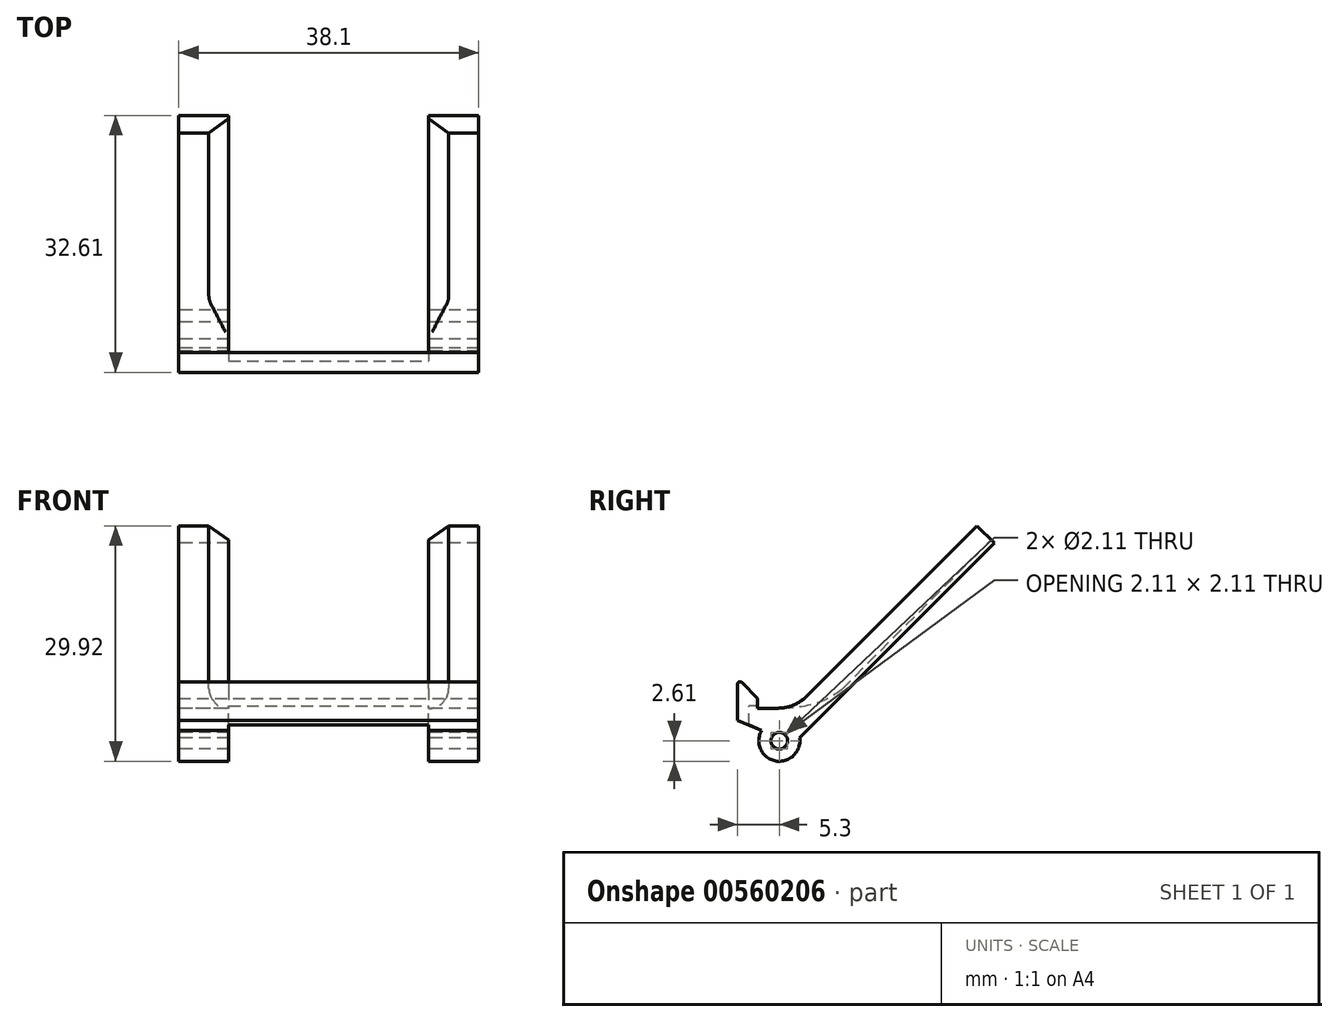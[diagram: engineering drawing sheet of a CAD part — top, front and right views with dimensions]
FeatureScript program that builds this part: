
annotation { "Feature Type Name" : "Feature", "Feature Type Description" : "" }
export const myFeature = defineFeature(function(context is Context, id is Id, definition is map)
    precondition{}
    {
        {
            var Q0;
            Q0=qCreatedBy(makeId("Right.planeOp"),FACE);
            var sketch = newSketch(context, id + "F0", { "sketchPlane" : qUnion([Q0])});
            skCircle(sketch, "E0", {"center": v(0, 0) * mm, "radius": 1.05 * mm});
            skArc(sketch, "E1.0", {"start": v(-2.24, 1.34) * mm, "mid": v(-0.5, -2.56) * mm, "end": v(2.58, 0.38) * mm});
            skLineSegment(sketch, "E2", {"start": v(0, 0) * mm, "end": v(18.4, 0) * mm, "construction": true});
            skLineSegment(sketch, "E3.0", {"start": v(1.94, 4.14) * mm, "end": v(25.1, 27.3) * mm});
            skLineSegment(sketch, "E4.0", {"start": v(2.58, 0.38) * mm, "end": v(27.3, 25.1) * mm});
            skLineSegment(sketch, "E5", {"start": v(25.1, 27.3) * mm, "end": v(27.3, 25.1) * mm});
            skLineSegment(sketch, "E6", {"start": v(-5.3, 2.58) * mm, "end": v(-5.3, 4.14) * mm});
            skLineSegment(sketch, "E7.0", {"start": v(1.94, 4.14) * mm, "end": v(-2.76, 4.14) * mm});
            skLineSegment(sketch, "E8", {"start": v(-5.3, 4.14) * mm, "end": v(-5.3, 7.95) * mm});
            skLineSegment(sketch, "E9", {"start": v(-5.3, 7.95) * mm, "end": v(-2.76, 7.95) * mm});
            skLineSegment(sketch, "E10", {"start": v(-2.76, 7.95) * mm, "end": v(-2.76, 4.14) * mm});
            skLineSegment(sketch, "E11", {"start": v(-5.3, 2.58) * mm, "end": v(-2.24, 1.34) * mm});
            skSolve(sketch);
        }
        {
            var Q0;
            Q0=makeQuery(id+"F0.imprint","IMPRINT",FACE,{"disambiguationData":[TD([[makeQuery(id+"F0.imprint","IMPRINT",EDGE,{"derivedFrom":sQuery(id+"F0.wireOp",EDGE,"E0")}),-1.0]])]});
            extrude(context, id + "F1", {"entities" : qUnion([Q0]), "endBound" : BoundingType.SYMMETRIC, "depth" : 38.1 * mm, "offsetDistance" : 25.4 * mm});
        }
        {
            var Q0;
            Q0=qCreatedBy(makeId("Top.planeOp"),FACE);
            var sketch = newSketch(context, id + "F2", { "sketchPlane" : qUnion([Q0])});
            skLineSegment(sketch, "E12", {"start": v(-6.35, 5.1) * mm, "end": v(-12.7, 5.1) * mm});
            skLineSegment(sketch, "E13", {"start": v(-12.7, 5.1) * mm, "end": v(-12.7, -3.87) * mm});
            skLineSegment(sketch, "E14", {"start": v(-12.7, -3.87) * mm, "end": v(12.7, -3.87) * mm});
            skLineSegment(sketch, "E15", {"start": v(-6.35, 5.1) * mm, "end": v(12.7, 5.1) * mm});
            skLineSegment(sketch, "E16", {"start": v(12.7, 5.1) * mm, "end": v(12.7, -3.87) * mm});
            skSolve(sketch);
        }
        {
            var Q0;
            Q0 = qSketchRegion(id + "F2", true);
            extrude(context, id + "F3", {"entities" : qUnion([Q0]), "operationType" : NewBodyOperationType.REMOVE, "endBound" : BoundingType.SYMMETRIC, "oppositeDirection" : true, "depth" : 8.9 * mm, "offsetDistance" : 25.4 * mm});
        }
        {
            var Q0;
            Q0=makeQuery(id+"F1.opExtrude","SWEPT_FACE",FACE,{"disambiguationData":[OSD([sQuery(id+"F0.wireOp",EDGE,"E4.0")])]});
            var sketch = newSketch(context, id + "F4", { "sketchPlane" : qUnion([Q0])});
            skLineSegment(sketch, "E17", {"start": v(-12.7, 37.06) * mm, "end": v(12.7, 37.06) * mm});
            skLineSegment(sketch, "E18", {"start": v(-12.7, 3.87) * mm, "end": v(12.7, 3.87) * mm});
            skLineSegment(sketch, "E19", {"start": v(-12.7, 3.87) * mm, "end": v(-12.7, 37.06) * mm});
            skLineSegment(sketch, "E20", {"start": v(12.7, 37.06) * mm, "end": v(12.7, 3.87) * mm});
            skSolve(sketch);
        }
        {
            var Q0;
            Q0 = qSketchRegion(id + "F4", true);
            extrude(context, id + "F5", {"entities" : qUnion([Q0]), "operationType" : NewBodyOperationType.REMOVE, "oppositeDirection" : true, "depth" : 12.7 * mm, "offsetDistance" : 25.4 * mm});
        }
        {
            var Q0;
            Q0=makeQuery(id+"F5.boolean.opBoolean","INTERSECT",EDGE,{"derivedFrom":[makeQuery(id+"F1.opExtrude","SWEPT_FACE",FACE,{"disambiguationData":[OSD([sQuery(id+"F0.wireOp",EDGE,"E3.0")])]}),makeQuery(id+"F5.opExtrude","SWEPT_FACE",FACE,{"disambiguationData":[OSD([sQuery(id+"F4.wireOp",EDGE,"E19")])]})]});
            var Q1;
            Q1=makeQuery(id+"F5.boolean.opBoolean","INTERSECT",EDGE,{"derivedFrom":[makeQuery(id+"F1.opExtrude","SWEPT_FACE",FACE,{"disambiguationData":[OSD([sQuery(id+"F0.wireOp",EDGE,"E3.0")])]}),makeQuery(id+"F5.opExtrude","SWEPT_FACE",FACE,{"disambiguationData":[OSD([sQuery(id+"F4.wireOp",EDGE,"E20")])]})]});
            chamfer(context, id + "F6", {"entities" : qUnion([Q0, Q1]), "width" : 2.54 * mm, "tangentPropagation" : true});
        }
        {
            var Q0;
            Q0=makeQuery(id+"F1.opExtrude","SWEPT_EDGE",EDGE,{"disambiguationData":[OSD([sQuery(id+"F0.wireOp",EDGE,"E9"),sQuery(id+"F0.wireOp",EDGE,"E10")])]});
            chamfer(context, id + "F7", {"entities" : qUnion([Q0]), "width" : 2.54 * mm, "tangentPropagation" : true});
        }
        {
            var Q0;
            Q0=makeQuery(id+"F7.opChamfer","BLEND_EDGE",EDGE,{"blendedFrom":[makeQuery(id+"F1.opExtrude","SWEPT_EDGE",EDGE,{"disambiguationData":[OSD([sQuery(id+"F0.wireOp",EDGE,"E9"),sQuery(id+"F0.wireOp",EDGE,"E10")])]}),makeQuery(id+"F1.opExtrude","SWEPT_FACE",FACE,{"disambiguationData":[OSD([sQuery(id+"F0.wireOp",EDGE,"E6"),sQuery(id+"F0.wireOp",EDGE,"E8")])]})],"blendedInto":[makeQuery(id+"F1.opExtrude","SWEPT_FACE",FACE,{"disambiguationData":[OSD([sQuery(id+"F0.wireOp",EDGE,"E6"),sQuery(id+"F0.wireOp",EDGE,"E8")])]})]});
            fillet(context, id + "F8", {"entities" : qUnion([Q0]), "radius" : 0.31 * mm, "tangentPropagation" : true, "allowEdgeOverflow" : false});
        }
        {
            var Q0;
            {var subQ0=sQuery(id+"F0.wireOp",EDGE,"E7.0");var subQ1=sQuery(id+"F0.wireOp",EDGE,"E3.0");Q0=makeQuery(id+"F3.boolean.opBoolean","SPLIT",EDGE,{"disambiguationData":[TD([makeQuery(id+"F3.opExtrude","SWEPT_FACE",FACE,{"disambiguationData":[OSD([sQuery(id+"F2.wireOp",EDGE,"E13")])]})])],"derivedFrom":makeQuery(id+"F1.opExtrude","SWEPT_EDGE",EDGE,{"disambiguationData":[OSD([subQ1,subQ0])]})});}
            var Q1;
            {var subQ0=sQuery(id+"F0.wireOp",EDGE,"E7.0");var subQ1=sQuery(id+"F0.wireOp",EDGE,"E3.0");Q1=makeQuery(id+"F3.boolean.opBoolean","SPLIT",EDGE,{"disambiguationData":[TD([makeQuery(id+"F3.opExtrude","SWEPT_FACE",FACE,{"disambiguationData":[OSD([sQuery(id+"F2.wireOp",EDGE,"E16")])]})])],"derivedFrom":makeQuery(id+"F1.opExtrude","SWEPT_EDGE",EDGE,{"disambiguationData":[OSD([subQ1,subQ0])]})});}
            var Q2;
            {var subQ1=sQuery(id+"F0.wireOp",EDGE,"E7.0");var subQ2=sQuery(id+"F0.wireOp",EDGE,"E3.0");var subQ3=makeQuery(id+"F1.opExtrude","SWEPT_FACE",FACE,{"disambiguationData":[OSD([subQ2])]});Q2=makeQuery(id+"F6.opChamfer","BLEND_EDGE",EDGE,{"blendedFrom":[makeQuery(id+"F5.boolean.opBoolean","INTERSECT",EDGE,{"derivedFrom":[subQ3,makeQuery(id+"F5.opExtrude","SWEPT_FACE",FACE,{"disambiguationData":[OSD([sQuery(id+"F4.wireOp",EDGE,"E19")])]})]}),makeQuery(id+"F3.boolean.opBoolean","SPLIT",FACE,{"disambiguationData":[TD([makeQuery(id+"F3.opExtrude","SWEPT_FACE",FACE,{"disambiguationData":[OSD([sQuery(id+"F2.wireOp",EDGE,"E16")])]})])],"derivedFrom":makeQuery(id+"F1.opExtrude","SWEPT_FACE",FACE,{"disambiguationData":[OSD([subQ1])]})})],"blendedInto":[makeQuery(id+"F3.boolean.opBoolean","SPLIT",FACE,{"disambiguationData":[TD([makeQuery(id+"F3.opExtrude","SWEPT_FACE",FACE,{"disambiguationData":[OSD([sQuery(id+"F2.wireOp",EDGE,"E16")])]})])],"derivedFrom":makeQuery(id+"F1.opExtrude","SWEPT_FACE",FACE,{"disambiguationData":[OSD([subQ1])]})})]});}
            var Q3;
            {var subQ1=sQuery(id+"F0.wireOp",EDGE,"E7.0");var subQ2=sQuery(id+"F0.wireOp",EDGE,"E3.0");var subQ3=makeQuery(id+"F1.opExtrude","SWEPT_FACE",FACE,{"disambiguationData":[OSD([subQ2])]});Q3=makeQuery(id+"F6.opChamfer","BLEND_EDGE",EDGE,{"blendedFrom":[makeQuery(id+"F5.boolean.opBoolean","INTERSECT",EDGE,{"derivedFrom":[subQ3,makeQuery(id+"F5.opExtrude","SWEPT_FACE",FACE,{"disambiguationData":[OSD([sQuery(id+"F4.wireOp",EDGE,"E20")])]})]}),makeQuery(id+"F3.boolean.opBoolean","SPLIT",FACE,{"disambiguationData":[TD([makeQuery(id+"F3.opExtrude","SWEPT_FACE",FACE,{"disambiguationData":[OSD([sQuery(id+"F2.wireOp",EDGE,"E13")])]})])],"derivedFrom":makeQuery(id+"F1.opExtrude","SWEPT_FACE",FACE,{"disambiguationData":[OSD([subQ1])]})})],"blendedInto":[makeQuery(id+"F3.boolean.opBoolean","SPLIT",FACE,{"disambiguationData":[TD([makeQuery(id+"F3.opExtrude","SWEPT_FACE",FACE,{"disambiguationData":[OSD([sQuery(id+"F2.wireOp",EDGE,"E13")])]})])],"derivedFrom":makeQuery(id+"F1.opExtrude","SWEPT_FACE",FACE,{"disambiguationData":[OSD([subQ1])]})})]});}
            fillet(context, id + "F9", {"entities" : qUnion([Q0, Q1, Q2, Q3]), "radius" : 5.08 * mm, "tangentPropagation" : true, "allowEdgeOverflow" : false});
        }
    });
